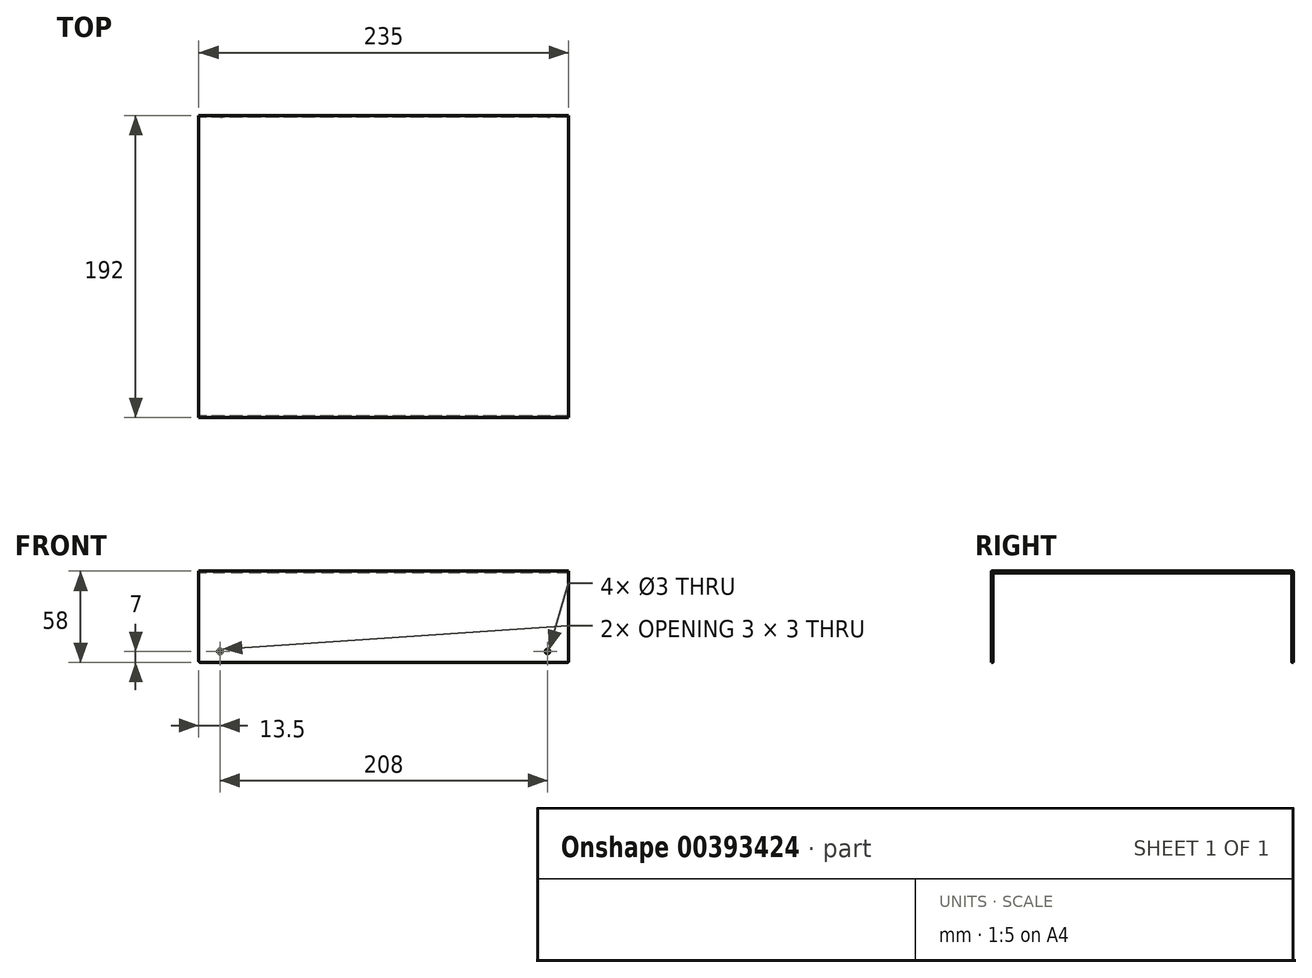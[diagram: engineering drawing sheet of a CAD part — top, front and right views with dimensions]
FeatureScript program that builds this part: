
annotation { "Feature Type Name" : "Feature", "Feature Type Description" : "" }
export const myFeature = defineFeature(function(context is Context, id is Id, definition is map)
    precondition{}
    {
        {
            var Q0;
            Q0=qCreatedBy(makeId("Top.planeOp"),FACE);
            var sketch = newSketch(context, id + "F0", { "sketchPlane" : qUnion([Q0])});
            skLineSegment(sketch, "E0.bottom", {"start": v(117.5, -95) * mm, "end": v(-117.5, -95) * mm});
            skLineSegment(sketch, "E0.top", {"start": v(117.5, 95) * mm, "end": v(-117.5, 95) * mm});
            skLineSegment(sketch, "E0.left", {"start": v(117.5, -95) * mm, "end": v(117.5, 95) * mm});
            skLineSegment(sketch, "E0.right", {"start": v(-117.5, -95) * mm, "end": v(-117.5, 95) * mm});
            skPoint(sketch, "E0.middle", {"position": v(0, 0) * mm});
            skSolve(sketch);
        }
        {
            var Q0;
            Q0=qSketchRegion(id+"F0",true);
            extrude(context, id + "F1", {"entities" : qUnion([Q0]), "depth" : 1 * mm});
        }
        {
            var Q0;
            Q0=makeQuery(id+"F1.opExtrude","CAP_FACE",FACE,{"disambiguationData":[OSD([sQuery(id+"F0.wireOp",EDGE,"E0.bottom"),sQuery(id+"F0.wireOp",EDGE,"E0.top"),sQuery(id+"F0.wireOp",EDGE,"E0.left"),sQuery(id+"F0.wireOp",EDGE,"E0.right")])],"isStart":false});
            var sketch = newSketch(context, id + "F2", { "sketchPlane" : qUnion([Q0])});
            skLineSegment(sketch, "E1.bottom", {"start": v(-117.5, -95) * mm, "end": v(117.5, -95) * mm});
            skLineSegment(sketch, "E1.top", {"start": v(-117.5, -96) * mm, "end": v(117.5, -96) * mm});
            skLineSegment(sketch, "E1.left", {"start": v(-117.5, -95) * mm, "end": v(-117.5, -96) * mm});
            skLineSegment(sketch, "E1.right", {"start": v(117.5, -95) * mm, "end": v(117.5, -96) * mm});
            skLineSegment(sketch, "E2.bottom", {"start": v(-117.5, 95) * mm, "end": v(117.5, 95) * mm});
            skLineSegment(sketch, "E2.top", {"start": v(-117.5, 96) * mm, "end": v(117.5, 96) * mm});
            skLineSegment(sketch, "E2.left", {"start": v(-117.5, 95) * mm, "end": v(-117.5, 96) * mm});
            skLineSegment(sketch, "E2.right", {"start": v(117.5, 95) * mm, "end": v(117.5, 96) * mm});
            skSolve(sketch);
        }
        {
            var Q0;
            Q0=qSketchRegion(id+"F2",true);
            extrude(context, id + "F3", {"entities" : qUnion([Q0]), "operationType" : NewBodyOperationType.ADD, "oppositeDirection" : true, "depth" : 58 * mm});
        }
        {
            var Q0;
            Q0=makeQuery(id+"F3.opExtrude","SWEPT_FACE",FACE,{"disambiguationData":[OSD([sQuery(id+"F2.wireOp",EDGE,"E1.top")])]});
            var sketch = newSketch(context, id + "F4", { "sketchPlane" : qUnion([Q0])});
            skCircle(sketch, "E3", {"center": v(-104, -50) * mm, "radius": 1.5 * mm});
            skCircle(sketch, "E4", {"center": v(104, -50) * mm, "radius": 1.5 * mm});
            skLineSegment(sketch, "E5.bottom", {"start": v(-19, -36.5) * mm, "end": v(-21, -36.5) * mm, "construction": true});
            skLineSegment(sketch, "E5.top", {"start": v(-19, -11.5) * mm, "end": v(-21, -11.5) * mm, "construction": true});
            skLineSegment(sketch, "E5.left", {"start": v(-19, -36.5) * mm, "end": v(-19, -11.5) * mm, "construction": true});
            skLineSegment(sketch, "E5.right", {"start": v(-21, -36.5) * mm, "end": v(-21, -11.5) * mm, "construction": true});
            skPoint(sketch, "E5.middle", {"position": v(-20, -24) * mm});
            skPoint(sketch, "E6.1.0.0", {"position": v(0, -24) * mm});
            skLineSegment(sketch, "E6.1.0.1", {"start": v(1, -36.5) * mm, "end": v(1, -11.5) * mm, "construction": true});
            skLineSegment(sketch, "E6.1.0.2", {"start": v(-1, -36.5) * mm, "end": v(-1, -11.5) * mm, "construction": true});
            skLineSegment(sketch, "E6.1.0.3", {"start": v(1, -36.5) * mm, "end": v(-1, -36.5) * mm, "construction": true});
            skLineSegment(sketch, "E6.1.0.4", {"start": v(1, -11.5) * mm, "end": v(-1, -11.5) * mm, "construction": true});
            skPoint(sketch, "E6.2.0.0", {"position": v(20, -24) * mm});
            skLineSegment(sketch, "E6.2.0.1", {"start": v(21, -36.5) * mm, "end": v(21, -11.5) * mm, "construction": true});
            skLineSegment(sketch, "E6.2.0.2", {"start": v(19, -36.5) * mm, "end": v(19, -11.5) * mm, "construction": true});
            skLineSegment(sketch, "E6.2.0.3", {"start": v(21, -36.5) * mm, "end": v(19, -36.5) * mm, "construction": true});
            skLineSegment(sketch, "E6.2.0.4", {"start": v(21, -11.5) * mm, "end": v(19, -11.5) * mm, "construction": true});
            skLineSegment(sketch, "E6.direction1", {"start": v(-21, -36.5) * mm, "end": v(-1, -36.5) * mm, "construction": true});
            skSolve(sketch);
        }
        {
            var Q0;
            Q0=qSketchRegion(id+"F4",true);
            extrude(context, id + "F5", {"entities" : qUnion([Q0]), "operationType" : NewBodyOperationType.REMOVE, "endBound" : BoundingType.THROUGH_ALL, "oppositeDirection" : true, "depth" : 25 * mm});
        }
        {
            var Q0;
            Q0=makeQuery(id+"F3.opExtrude","CAP_EDGE",EDGE,{"disambiguationData":[OSD([sQuery(id+"F2.wireOp",EDGE,"E1.top")])],"isStart":true});
            var Q1;
            Q1=makeQuery(id+"F3.opExtrude","CAP_EDGE",EDGE,{"disambiguationData":[OSD([sQuery(id+"F2.wireOp",EDGE,"E2.top")])],"isStart":true});
            var Q2;
            Q2=makeQuery(id+"F1.opExtrude","CAP_EDGE",EDGE,{"disambiguationData":[OSD([sQuery(id+"F0.wireOp",EDGE,"E0.bottom")])],"isStart":true});
            var Q3;
            Q3=makeQuery(id+"F1.opExtrude","CAP_EDGE",EDGE,{"disambiguationData":[OSD([sQuery(id+"F0.wireOp",EDGE,"E0.top")])],"isStart":true});
            fillet(context, id + "F6", {"entities" : qUnion([Q0, Q1, Q2, Q3]), "radius" : 0.5 * mm, "tangentPropagation" : true, "allowEdgeOverflow" : false});
        }
        {
            var Q0;
            Q0=makeQuery(id+"F3.opExtrude","CAP_EDGE",EDGE,{"disambiguationData":[OSD([sQuery(id+"F2.wireOp",EDGE,"E1.left")])],"isStart":false});
            var Q1;
            Q1=makeQuery(id+"F3.opExtrude","CAP_EDGE",EDGE,{"disambiguationData":[OSD([sQuery(id+"F2.wireOp",EDGE,"E1.right")])],"isStart":false});
            var Q2;
            Q2=makeQuery(id+"F3.opExtrude","CAP_EDGE",EDGE,{"disambiguationData":[OSD([sQuery(id+"F2.wireOp",EDGE,"E2.right")])],"isStart":false});
            var Q3;
            Q3=makeQuery(id+"F3.opExtrude","CAP_EDGE",EDGE,{"disambiguationData":[OSD([sQuery(id+"F2.wireOp",EDGE,"E2.left")])],"isStart":false});
            fillet(context, id + "F7", {"entities" : qUnion([Q0, Q1, Q2, Q3]), "radius" : 1 * mm, "tangentPropagation" : true, "allowEdgeOverflow" : false});
        }
    });
